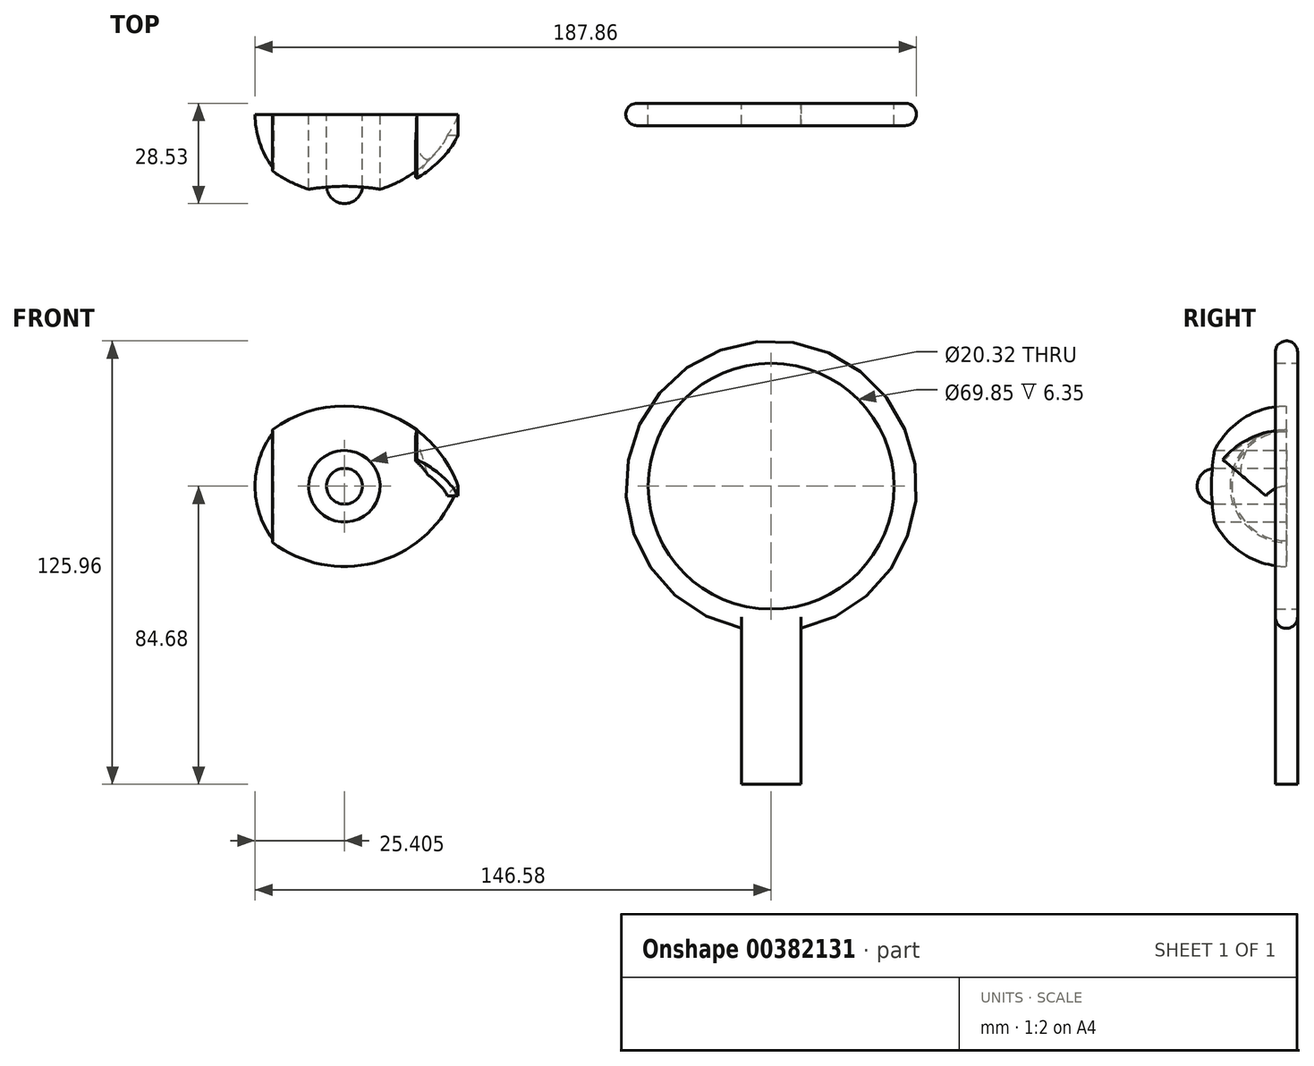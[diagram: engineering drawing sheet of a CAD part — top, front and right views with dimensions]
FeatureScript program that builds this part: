
annotation { "Feature Type Name" : "Feature", "Feature Type Description" : "" }
export const myFeature = defineFeature(function(context is Context, id is Id, definition is map)
    precondition{}
    {
        {
            var Q0;
            Q0=qCreatedBy(makeId("Front.planeOp"),FACE);
            var sketch = newSketch(context, id + "F0", { "sketchPlane" : qUnion([Q0])});
            skArc(sketch, "E0", {"start": v(-12.7, 0) * mm, "mid": v(-44.98, 22.8) * mm, "end": v(-77.25, 0) * mm});
            skLineSegment(sketch, "E1", {"start": v(-77.25, 0) * mm, "end": v(-12.7, 0) * mm});
            skArc(sketch, "E2", {"start": v(-65.48, 15.99) * mm, "mid": v(-44.98, 5.35) * mm, "end": v(-24.47, 15.99) * mm});
            skPoint(sketch, "E2.centerSnap0", {"position": v(-44.98, 22.8) * mm});
            skArc(sketch, "E3", {"start": v(-65.11, 15.48) * mm, "mid": v(-44.98, -25.4) * mm, "end": v(-24.84, 15.48) * mm});
            skLineSegment(sketch, "E4", {"start": v(-77.25, -7.62) * mm, "end": v(-12.7, -7.62) * mm});
            skCircle(sketch, "E5", {"center": v(76.2, 0) * mm, "radius": 34.93 * mm});
            skArc(sketch, "E6", {"start": v(84.67, -40.4) * mm, "mid": v(76.2, 41.28) * mm, "end": v(67.73, -40.4) * mm});
            skLineSegment(sketch, "E7.top", {"start": v(84.67, -84.68) * mm, "end": v(67.73, -84.68) * mm});
            skLineSegment(sketch, "E7.left", {"start": v(84.67, -33.88) * mm, "end": v(84.67, -84.68) * mm});
            skLineSegment(sketch, "E7.right", {"start": v(67.73, -33.88) * mm, "end": v(67.73, -84.68) * mm});
            skCircle(sketch, "E8", {"center": v(-44.98, 0) * mm, "radius": 5.08 * mm});
            skSolve(sketch);
        }
        {
            var Q0;
            {var subQ0=sQuery(id+"F0.wireOp",EDGE,"E2");var subQ1=sQuery(id+"F0.wireOp",EDGE,"E0");var subQ2=makeQuery(id+"F0.imprint","INTERSECT",VERTEX,{"disambiguationData":[OD(0.0)],"derivedFrom":[subQ1,subQ0]});Q0=makeQuery(id+"F0.imprint","IMPRINT",FACE,{"disambiguationData":[TD([[makeQuery(id+"F0.imprint","IMPRINT",EDGE,{"disambiguationData":[TD([[subQ2,-1.0]])],"derivedFrom":subQ1}),1.0]])]});}
            var Q1;
            {var subQ0=sQuery(id+"F0.wireOp",EDGE,"E1");Q1=makeQuery(id+"F0.imprint","IMPRINT",FACE,{"disambiguationData":[TD([[makeQuery(id+"F0.imprint","IMPRINT",EDGE,{"derivedFrom":subQ0}),1.0]])]});}
            var Q2;
            {var subQ0=sQuery(id+"F0.wireOp",EDGE,"E2");var subQ1=sQuery(id+"F0.wireOp",EDGE,"E0");var subQ2=makeQuery(id+"F0.imprint","INTERSECT",VERTEX,{"disambiguationData":[OD(0.0)],"derivedFrom":[subQ1,subQ0]});Q2=makeQuery(id+"F0.imprint","IMPRINT",FACE,{"disambiguationData":[TD([[makeQuery(id+"F0.imprint","IMPRINT",EDGE,{"disambiguationData":[TD([[subQ2,1.0]])],"derivedFrom":subQ1}),1.0]])]});}
            var Q3;
            {var subQ0=sQuery(id+"F0.wireOp",EDGE,"E1");var subQ1=sQuery(id+"F0.wireOp",EDGE,"E0");var subQ2=makeQuery(id+"F0.imprint","INTERSECT",VERTEX,{"disambiguationData":[OD(0.0)],"derivedFrom":[subQ1,subQ0]});Q3=makeQuery(id+"F0.imprint","IMPRINT",FACE,{"disambiguationData":[TD([[makeQuery(id+"F0.imprint","IMPRINT",EDGE,{"disambiguationData":[TD([[subQ2,-1.0]])],"derivedFrom":subQ1}),1.0]])]});}
            var Q4;
            Q4=sQuery(id+"F0.wireOp",EDGE,"E1");
            revolve(context, id + "F1", {"entities" : qUnion([Q0, Q1, Q2, Q3]), "axis" : qUnion([Q4]), "revolveType" : RevolveType.ONE_DIRECTION, "angle" : 180 * degree});
        }
        {
            var Q0;
            Q0=sQuery(id+"F0.wireOp",VERTEX,"E3.center");
            var Q1;
            Q1=makeQuery(id+"F1.opRevolve","SWEPT_BODY",BODY,{"disambiguationData":[OSD([sQuery(id+"F0.wireOp",EDGE,"E0"),sQuery(id+"F0.wireOp",EDGE,"E1")])]});
            hole(context, id + "F2", {"style" : HoleStyle.SIMPLE, "endStyle" : HoleEndStyle.THROUGH, "oppositeDirection" : true, "holeDiameter" : 20.32 * mm, "isTappedThrough" : true, "tappedDepth" : 12.7 * mm, "tapClearance" : 3, "locations" : qUnion([Q0]), "scope" : qUnion([Q1])});
        }
        {
            var Q0;
            {var subQ0=sQuery(id+"F0.wireOp",EDGE,"E2");var subQ1=sQuery(id+"F0.wireOp",EDGE,"E0");var subQ2=makeQuery(id+"F0.imprint","INTERSECT",VERTEX,{"disambiguationData":[OD(0.0)],"derivedFrom":[subQ1,subQ0]});Q0=makeQuery(id+"F0.imprint","IMPRINT",FACE,{"disambiguationData":[TD([[makeQuery(id+"F0.imprint","IMPRINT",EDGE,{"disambiguationData":[TD([[subQ2,1.0]])],"derivedFrom":subQ1}),1.0]])]});}
            var Q1;
            Q1=sQuery(id+"F0.wireOp",EDGE,"E4");
            revolve(context, id + "F3", {"operationType" : NewBodyOperationType.ADD, "entities" : qUnion([Q0]), "axis" : qUnion([Q1]), "revolveType" : RevolveType.ONE_DIRECTION, "angle" : 50 * degree});
        }
        {
            var Q0;
            Q0=makeQuery(id+"F0.imprint","IMPRINT",FACE,{"disambiguationData":[TD([[makeQuery(id+"F0.imprint","IMPRINT",EDGE,{"derivedFrom":sQuery(id+"F0.wireOp",EDGE,"E5")}),-1.0]])]});
            extrude(context, id + "F4", {"entities" : qUnion([Q0]), "endBound" : BoundingType.SYMMETRIC, "depth" : 6.35 * mm});
        }
        {
            var Q0;
            Q0=makeQuery(id+"F4.opExtrude","CAP_EDGE",EDGE,{"disambiguationData":[OSD([sQuery(id+"F0.wireOp",EDGE,"E6")])],"isStart":false});
            var Q1;
            Q1=makeQuery(id+"F4.opExtrude","CAP_EDGE",EDGE,{"disambiguationData":[OSD([sQuery(id+"F0.wireOp",EDGE,"E6")])],"isStart":true});
            fillet(context, id + "F5", {"entities" : qUnion([Q0, Q1]), "radius" : 3.17 * mm, "tangentPropagation" : true, "allowEdgeOverflow" : false});
        }
        {
            var Q0;
            {var subQ5=sQuery(id+"F0.wireOp",EDGE,"E7.top");Q0=makeQuery(id+"F0.imprint","IMPRINT",FACE,{"disambiguationData":[TD([[makeQuery(id+"F0.imprint","IMPRINT",EDGE,{"derivedFrom":subQ5}),-1.0]])]});}
            extrude(context, id + "F6", {"entities" : qUnion([Q0]), "operationType" : NewBodyOperationType.ADD, "endBound" : BoundingType.SYMMETRIC, "depth" : 6.35 * mm});
        }
        {
            var Q0;
            {var subQ0=sQuery(id+"F0.wireOp",EDGE,"E8");var subQ1=sQuery(id+"F0.wireOp",EDGE,"E1");var subQ2=makeQuery(id+"F0.imprint","INTERSECT",VERTEX,{"disambiguationData":[OD(0.0)],"derivedFrom":[subQ1,subQ0]});Q0=makeQuery(id+"F0.imprint","IMPRINT",FACE,{"disambiguationData":[TD([[makeQuery(id+"F0.imprint","IMPRINT",EDGE,{"disambiguationData":[TD([[subQ2,-1.0]])],"derivedFrom":subQ1}),1.0]])]});}
            var Q1;
            {var subQ0=sQuery(id+"F0.wireOp",EDGE,"E8");var subQ1=sQuery(id+"F0.wireOp",EDGE,"E1");var subQ2=makeQuery(id+"F0.imprint","INTERSECT",VERTEX,{"disambiguationData":[OD(0.0)],"derivedFrom":[subQ1,subQ0]});Q1=makeQuery(id+"F0.imprint","IMPRINT",FACE,{"disambiguationData":[TD([[makeQuery(id+"F0.imprint","IMPRINT",EDGE,{"disambiguationData":[TD([[subQ2,-1.0]])],"derivedFrom":subQ1}),-1.0]])]});}
            extrude(context, id + "F7", {"entities" : qUnion([Q0, Q1]), "operationType" : NewBodyOperationType.ADD, "depth" : 25.35 * mm});
        }
        {
            var Q0;
            Q0=makeQuery(id+"F7.opExtrude","CAP_EDGE",EDGE,{"disambiguationData":[OSD([sQuery(id+"F0.wireOp",EDGE,"E8")])],"isStart":false});
            fillet(context, id + "F8", {"entities" : qUnion([Q0]), "radius" : 5.08 * mm, "tangentPropagation" : true, "allowEdgeOverflow" : false});
        }
    });
